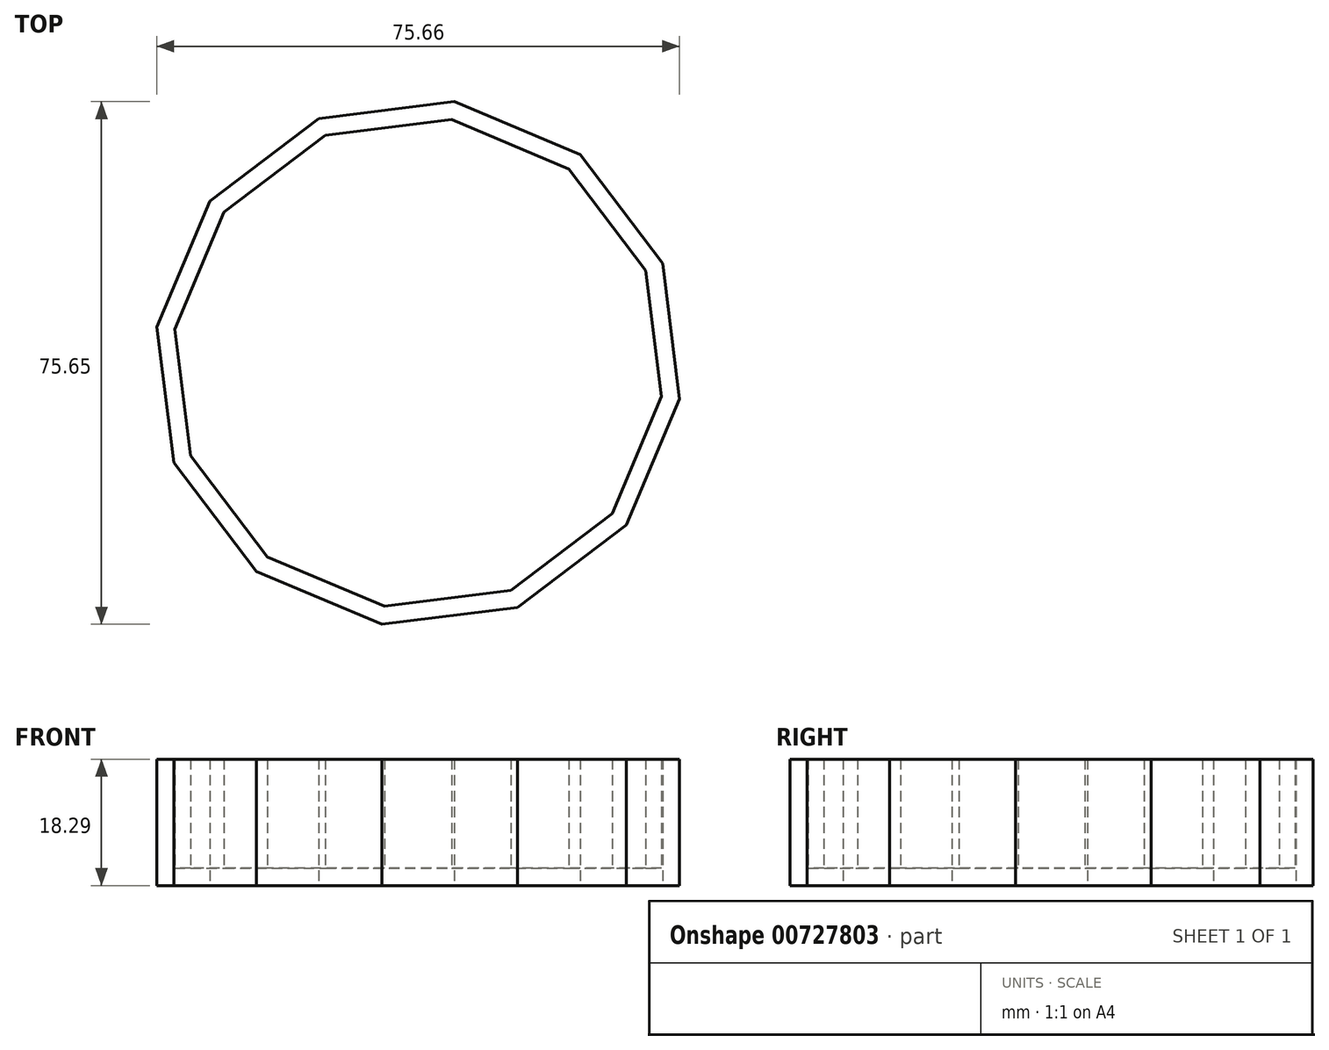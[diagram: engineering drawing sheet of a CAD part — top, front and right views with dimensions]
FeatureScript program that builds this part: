
annotation { "Feature Type Name" : "Feature", "Feature Type Description" : "" }
export const myFeature = defineFeature(function(context is Context, id is Id, definition is map)
    precondition{}
    {
        {
            var Q0;
            Q0=qCreatedBy(makeId("Top.planeOp"),FACE);
            var sketch = newSketch(context, id + "F0", { "sketchPlane" : qUnion([Q0])});
            skCircle(sketch, "E0.cCircle", {"center": v(0, 6.29) * mm, "radius": 36.88 * mm, "construction": true});
            skLineSegment(sketch, "E0.0", {"start": v(-14.4, 41.65) * mm, "end": v(5.21, 44.11) * mm});
            skLineSegment(sketch, "E0.1", {"start": v(5.21, 44.11) * mm, "end": v(23.43, 36.44) * mm});
            skLineSegment(sketch, "E0.2", {"start": v(23.43, 36.44) * mm, "end": v(35.37, 20.69) * mm});
            skLineSegment(sketch, "E0.3", {"start": v(35.37, 20.69) * mm, "end": v(37.83, 1.07) * mm});
            skLineSegment(sketch, "E0.4", {"start": v(37.83, 1.07) * mm, "end": v(30.15, -17.14) * mm});
            skLineSegment(sketch, "E0.5", {"start": v(30.15, -17.14) * mm, "end": v(14.4, -29.08) * mm});
            skLineSegment(sketch, "E0.6", {"start": v(14.4, -29.08) * mm, "end": v(-5.21, -31.54) * mm});
            skLineSegment(sketch, "E0.7", {"start": v(-5.21, -31.54) * mm, "end": v(-23.43, -23.87) * mm});
            skLineSegment(sketch, "E0.8", {"start": v(-23.43, -23.87) * mm, "end": v(-35.37, -8.11) * mm});
            skLineSegment(sketch, "E0.9", {"start": v(-35.37, -8.11) * mm, "end": v(-37.83, 11.5) * mm});
            skLineSegment(sketch, "E0.10", {"start": v(-37.83, 11.5) * mm, "end": v(-30.15, 29.72) * mm});
            skLineSegment(sketch, "E0.11", {"start": v(-30.15, 29.72) * mm, "end": v(-14.4, 41.65) * mm});
            skPoint(sketch, "E0.0.midPoint", {"position": v(-4.6, 42.88) * mm});
            skSolve(sketch);
        }
        {
            var Q0;
            Q0=makeQuery(id+"F0.imprint","IMPRINT",FACE,{"disambiguationData":[TD([[makeQuery(id+"F0.imprint","IMPRINT",EDGE,{"derivedFrom":sQuery(id+"F0.wireOp",EDGE,"E0.0")}),-1.0]])]});
            extrude(context, id + "F1", {"entities" : qUnion([Q0]), "depth" : 18.29 * mm, "offsetDistance" : 25.4 * mm});
        }
        {
            var Q0;
            Q0=makeQuery(id+"F1.opExtrude","CAP_FACE",FACE,{"disambiguationData":[OSD([sQuery(id+"F0.wireOp",EDGE,"E0.0"),sQuery(id+"F0.wireOp",EDGE,"E0.1"),sQuery(id+"F0.wireOp",EDGE,"E0.2"),sQuery(id+"F0.wireOp",EDGE,"E0.3"),sQuery(id+"F0.wireOp",EDGE,"E0.4"),sQuery(id+"F0.wireOp",EDGE,"E0.5"),sQuery(id+"F0.wireOp",EDGE,"E0.6"),sQuery(id+"F0.wireOp",EDGE,"E0.7"),sQuery(id+"F0.wireOp",EDGE,"E0.8"),sQuery(id+"F0.wireOp",EDGE,"E0.9"),sQuery(id+"F0.wireOp",EDGE,"E0.10"),sQuery(id+"F0.wireOp",EDGE,"E0.11")])],"isStart":false});
            shell(context, id + "F2", {"entities" : qUnion([Q0]), "thickness" : 177.8 * mm});
        }
        {
            var Q0;
            Q0=makeQuery(id+"F1.opExtrude","CAP_FACE",FACE,{"disambiguationData":[OSD([sQuery(id+"F0.wireOp",EDGE,"E0.0"),sQuery(id+"F0.wireOp",EDGE,"E0.1"),sQuery(id+"F0.wireOp",EDGE,"E0.2"),sQuery(id+"F0.wireOp",EDGE,"E0.3"),sQuery(id+"F0.wireOp",EDGE,"E0.4"),sQuery(id+"F0.wireOp",EDGE,"E0.5"),sQuery(id+"F0.wireOp",EDGE,"E0.6"),sQuery(id+"F0.wireOp",EDGE,"E0.7"),sQuery(id+"F0.wireOp",EDGE,"E0.8"),sQuery(id+"F0.wireOp",EDGE,"E0.9"),sQuery(id+"F0.wireOp",EDGE,"E0.10"),sQuery(id+"F0.wireOp",EDGE,"E0.11")])],"isStart":false});
            shell(context, id + "F3", {"entities" : qUnion([Q0]), "thickness" : 2.54 * mm});
        }
    });
